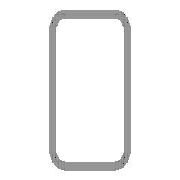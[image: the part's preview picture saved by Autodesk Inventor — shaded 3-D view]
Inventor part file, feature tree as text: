
AUTODESK INVENTOR PART (.ipt)
format: ipt  version: 2025.3 (Build 293356000, 356)  size: 150,016 bytes
history: native  units: mm (DEFAULTED — no unit token found)
features: other x4, plane x3, split x2, sketch x1
ambient origin geometry x8: Origin, YZ Plane, XZ Plane, XY Plane, X Axis, Y Axis, Z Axis, Center Point
bodies: Solid1 (feature_tree), Body (feature_tree)
feature tree (10):
  parser-record x1  (decoder bookkeeping rows leaked as tree rows — omitted from the tree; the rows remain in map.json)
  other  "Driven Length"
  other  "Start Plane"
  other  "End Plane"
  plane  "Work Plane4"
  split  "Split1"
  plane  "Work Plane5"
  split  "Split2"
  sketch  "Sketch3"  dims[d3=3151.269837mm d4=0.0mm d7=4.0mm d9=20.0mm d11=40.0mm d12=2.0mm d13=0.0mm d14=3151.269837mm d15=10.0mm d16=20.0mm d17=90.0deg d18=3151.269837mm]
  plane  "Work Plane3"
